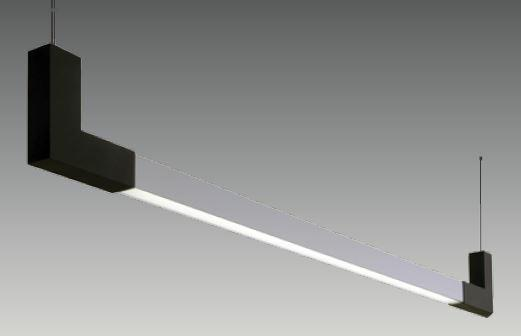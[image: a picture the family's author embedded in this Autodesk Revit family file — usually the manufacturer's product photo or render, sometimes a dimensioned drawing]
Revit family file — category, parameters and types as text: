
# Revit family: SD 1800 PLU
name_source: partatom
category: Lighting Fixtures
revit_build: Autodesk Revit 2017 (Build: 20160225_1515(x64)
units: mm (PartAtom-declared; Revit-internal decimal feet)

## family parameters
Cut with Voids When Loaded = No
Host = Face
Light Source = Yes
Part Type = Normal
Room Calculation Point = No
Round Connector Dimension = Use Diameter
Shared = No

## types (2) — shared parameters
Color Filter = 16777215
Default Elevation = 1219 mm
Dimming Lamp Color Temperature Shift = <None>
Emit Shape Visible in Rendering = Yes
Emit from Rectangle Length = 40 mm  [stored 0.131234 ft]
Emit from Rectangle Width = 1400 mm  [stored 4.59318 ft]
Light Source Symbol Size = 610 mm
Manufacturer = ARLIGHT
Type Image = SD 1800 PLU.JPG
Wattage Comments = 54W

## type names (no varying parameters)
- SDPLU.1800.54.30
- SDPLU.1800.54.40

note: [stored X ft] marks values corroborated as IEEE doubles in the binary element streams (Revit-internal decimal feet)

## geometry (parser evidence)
native form markers: Sweep x3
no freeform markers — native parametric forms only
